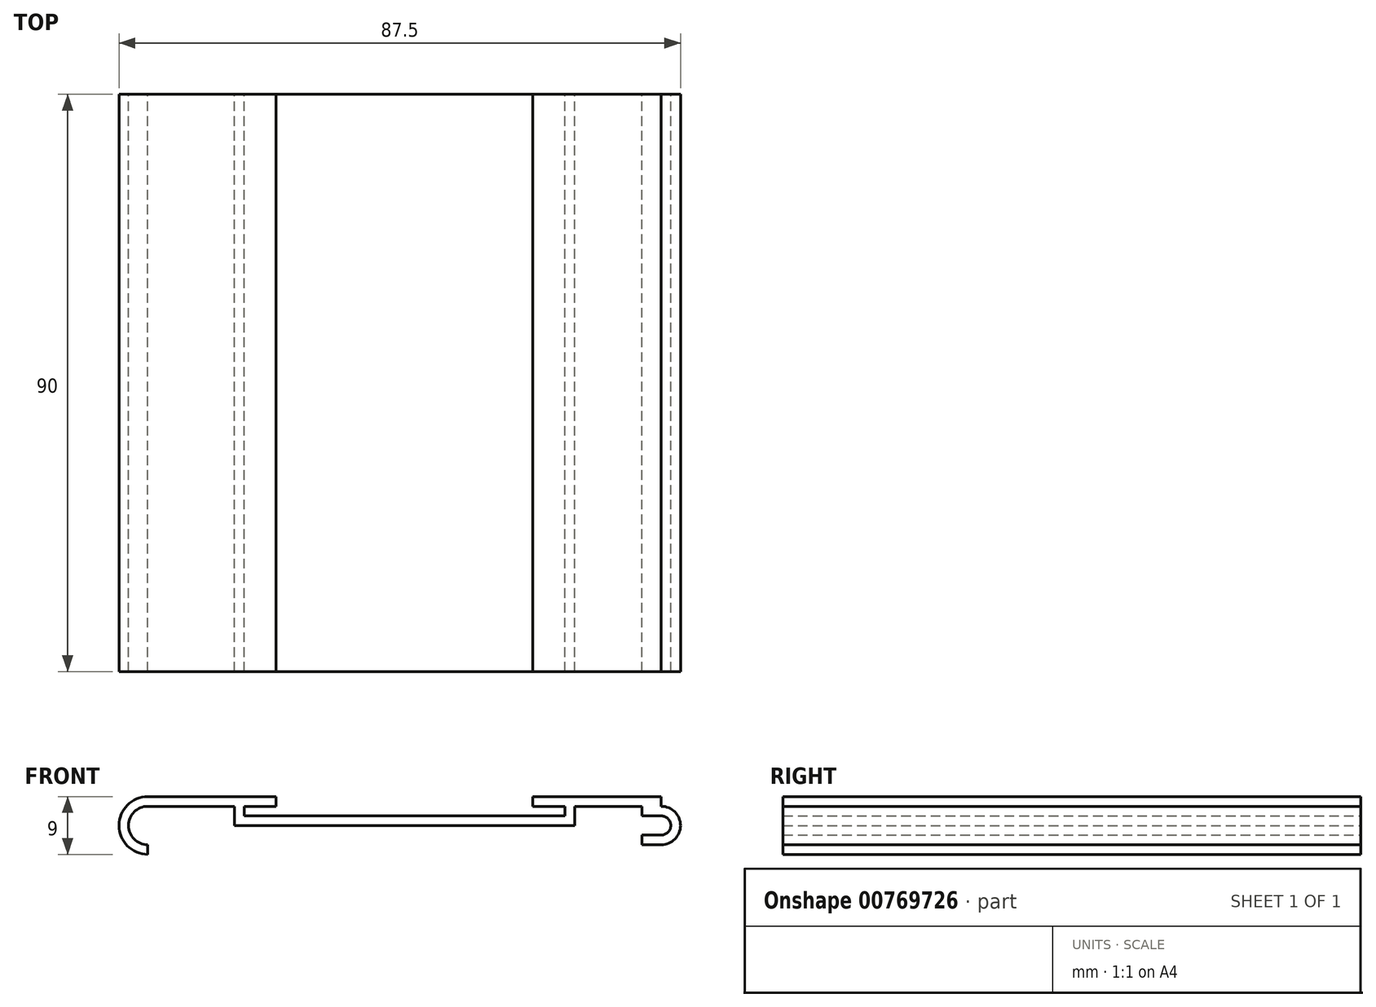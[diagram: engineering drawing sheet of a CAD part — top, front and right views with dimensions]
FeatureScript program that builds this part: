
annotation { "Feature Type Name" : "Feature", "Feature Type Description" : "" }
export const myFeature = defineFeature(function(context is Context, id is Id, definition is map)
    precondition{}
    {
        {
            var Q0;
            Q0=qCreatedBy(makeId("Front.planeOp"),FACE);
            var sketch = newSketch(context, id + "F0", { "sketchPlane" : qUnion([Q0])});
            skLineSegment(sketch, "E0.bottom", {"start": v(40, 4.5) * mm, "end": v(-40, 4.5) * mm});
            skLineSegment(sketch, "E0.top", {"start": v(40, -4.5) * mm, "end": v(-40, -4.5) * mm});
            skPoint(sketch, "E0.middle", {"position": v(0, 0) * mm});
            skArc(sketch, "E1", {"start": v(-40, 4.5) * mm, "mid": v(-44.5, 0) * mm, "end": v(-40, -4.5) * mm});
            skArc(sketch, "E2", {"start": v(40, 4.5) * mm, "mid": v(44.5, 0) * mm, "end": v(40, -4.5) * mm});
            skSolve(sketch);
        }
        {
            var Q0;
            Q0 = qSketchRegion(id + "F0", true);
            extrude(context, id + "F1", {"entities" : qUnion([Q0]), "depth" : 90 * mm, "offsetDistance" : 25 * mm});
        }
        {
            var Q0;
            Q0=qCreatedBy(makeId("Front.planeOp"),FACE);
            var sketch = newSketch(context, id + "F2", { "sketchPlane" : qUnion([Q0])});
            skLineSegment(sketch, "E3.bottom", {"start": v(-25, 4.5) * mm, "end": v(25, 4.5) * mm});
            skLineSegment(sketch, "E3.top", {"start": v(-25, 1.5) * mm, "end": v(25, 1.5) * mm});
            skLineSegment(sketch, "E3.left", {"start": v(-25, 4.5) * mm, "end": v(-25, 1.5) * mm});
            skLineSegment(sketch, "E3.right", {"start": v(25, 4.5) * mm, "end": v(25, 1.5) * mm});
            skPoint(sketch, "E4", {"position": v(0, 4.5) * mm});
            skSolve(sketch);
        }
        {
            var Q0;
            Q0 = qSketchRegion(id + "F2", true);
            extrude(context, id + "F3", {"entities" : qUnion([Q0]), "operationType" : NewBodyOperationType.REMOVE, "endBound" : BoundingType.THROUGH_ALL, "depth" : 25 * mm, "offsetDistance" : 25 * mm});
        }
        {
            var Q0;
            Q0=makeQuery(id+"F1.opExtrude","CAP_FACE",FACE,{"disambiguationData":[OSD([sQuery(id+"F0.wireOp",EDGE,"E0.bottom"),sQuery(id+"F0.wireOp",EDGE,"E0.top"),sQuery(id+"F0.wireOp",EDGE,"E1"),sQuery(id+"F0.wireOp",EDGE,"E2")])],"isStart":false});
            var Q1;
            Q1=makeQuery(id+"F1.opExtrude","CAP_FACE",FACE,{"disambiguationData":[OSD([sQuery(id+"F0.wireOp",EDGE,"E0.bottom"),sQuery(id+"F0.wireOp",EDGE,"E0.top"),sQuery(id+"F0.wireOp",EDGE,"E1"),sQuery(id+"F0.wireOp",EDGE,"E2")])],"isStart":true});
            shell(context, id + "F4", {"entities" : qUnion([Q0, Q1]), "thickness" : 1.5 * mm});
        }
        {
            var Q0;
            Q0=qCreatedBy(makeId("Front.planeOp"),FACE);
            var sketch = newSketch(context, id + "F5", { "sketchPlane" : qUnion([Q0])});
            skLineSegment(sketch, "E5.0", {"start": v(40, -3) * mm, "end": v(-40, -3) * mm});
            skLineSegment(sketch, "E6.0", {"start": v(40, -4.5) * mm, "end": v(-40, -4.5) * mm});
            skArc(sketch, "E7.0", {"start": v(40, 3) * mm, "mid": v(43, 0) * mm, "end": v(40, -3) * mm});
            skArc(sketch, "E8.0", {"start": v(40, 4.5) * mm, "mid": v(44.5, 0) * mm, "end": v(40, -4.5) * mm});
            skLineSegment(sketch, "E9", {"start": v(-40, -3) * mm, "end": v(-40, -4.5) * mm});
            skLineSegment(sketch, "E10", {"start": v(40, 4.5) * mm, "end": v(40, 3) * mm});
            skSolve(sketch);
        }
        {
            var Q0;
            Q0 = qSketchRegion(id + "F5", true);
            extrude(context, id + "F6", {"entities" : qUnion([Q0]), "operationType" : NewBodyOperationType.REMOVE, "endBound" : BoundingType.THROUGH_ALL, "depth" : 25 * mm, "offsetDistance" : 25 * mm});
        }
        {
            var Q0;
            Q0=qCreatedBy(makeId("Front.planeOp"),FACE);
            var sketch = newSketch(context, id + "F7", { "sketchPlane" : qUnion([Q0])});
            skArc(sketch, "E11", {"start": v(40, -3) * mm, "mid": v(43, 0) * mm, "end": v(40, 3) * mm});
            skLineSegment(sketch, "E12.0", {"start": v(40, 3) * mm, "end": v(37, 3) * mm});
            skLineSegment(sketch, "E13", {"start": v(37, 0) * mm, "end": v(37, 3) * mm});
            skPoint(sketch, "E14.orphan", {"position": v(26.5, 3) * mm});
            skLineSegment(sketch, "E15.bottom", {"start": v(-25, 4.5) * mm, "end": v(-20, 4.5) * mm});
            skLineSegment(sketch, "E15.top", {"start": v(-25, 3) * mm, "end": v(-20, 3) * mm});
            skLineSegment(sketch, "E15.left", {"start": v(-25, 4.5) * mm, "end": v(-25, 3) * mm});
            skLineSegment(sketch, "E15.right", {"start": v(-20, 4.5) * mm, "end": v(-20, 3) * mm});
            skLineSegment(sketch, "E16", {"start": v(0, 0) * mm, "end": v(0, -6.8) * mm, "construction": true});
            skLineSegment(sketch, "E17.MirrorCS", {"start": v(25, 4.5) * mm, "end": v(20, 4.5) * mm});
            skLineSegment(sketch, "E18.MirrorCS", {"start": v(25, 3) * mm, "end": v(20, 3) * mm});
            skLineSegment(sketch, "E19.MirrorCS", {"start": v(25, 4.5) * mm, "end": v(25, 3) * mm});
            skLineSegment(sketch, "E20.MirrorCS", {"start": v(20, 4.5) * mm, "end": v(20, 3) * mm});
            skLineSegment(sketch, "E21.MirrorCS", {"start": v(40, -3) * mm, "end": v(37, -3) * mm});
            skLineSegment(sketch, "E22.MirrorCS", {"start": v(37, 0) * mm, "end": v(37, -3) * mm});
            skSolve(sketch);
        }
        {
            var Q0;
            Q0 = qSketchRegion(id + "F7", true);
            var Q1;
            Q1=makeQuery(id+"F1.opExtrude","CAP_FACE",FACE,{"disambiguationData":[OSD([sQuery(id+"F0.wireOp",EDGE,"E0.bottom"),sQuery(id+"F0.wireOp",EDGE,"E0.top"),sQuery(id+"F0.wireOp",EDGE,"E1"),sQuery(id+"F0.wireOp",EDGE,"E2")])],"isStart":false});
            extrude(context, id + "F8", {"entities" : qUnion([Q0]), "operationType" : NewBodyOperationType.ADD, "endBound" : BoundingType.UP_TO_SURFACE, "depth" : 25 * mm, "endBoundEntityFace" : qUnion([Q1]), "offsetDistance" : 25 * mm});
        }
        {
            var Q0;
            Q0=qCreatedBy(makeId("Front.planeOp"),FACE);
            var sketch = newSketch(context, id + "F9", { "sketchPlane" : qUnion([Q0])});
            skLineSegment(sketch, "E23.0", {"start": v(40, -1.5) * mm, "end": v(37, -1.5) * mm});
            skArc(sketch, "E24", {"start": v(40, -1.5) * mm, "mid": v(41.5, 0) * mm, "end": v(40, 1.5) * mm});
            skLineSegment(sketch, "E25", {"start": v(37, -1.5) * mm, "end": v(37, 1.5) * mm});
            skLineSegment(sketch, "E26", {"start": v(37, 1.5) * mm, "end": v(40, 1.5) * mm});
            skSolve(sketch);
        }
        {
            var Q0;
            Q0 = qSketchRegion(id + "F9", true);
            extrude(context, id + "F10", {"entities" : qUnion([Q0]), "operationType" : NewBodyOperationType.REMOVE, "endBound" : BoundingType.THROUGH_ALL, "depth" : 25 * mm, "offsetDistance" : 25 * mm});
        }
    });
